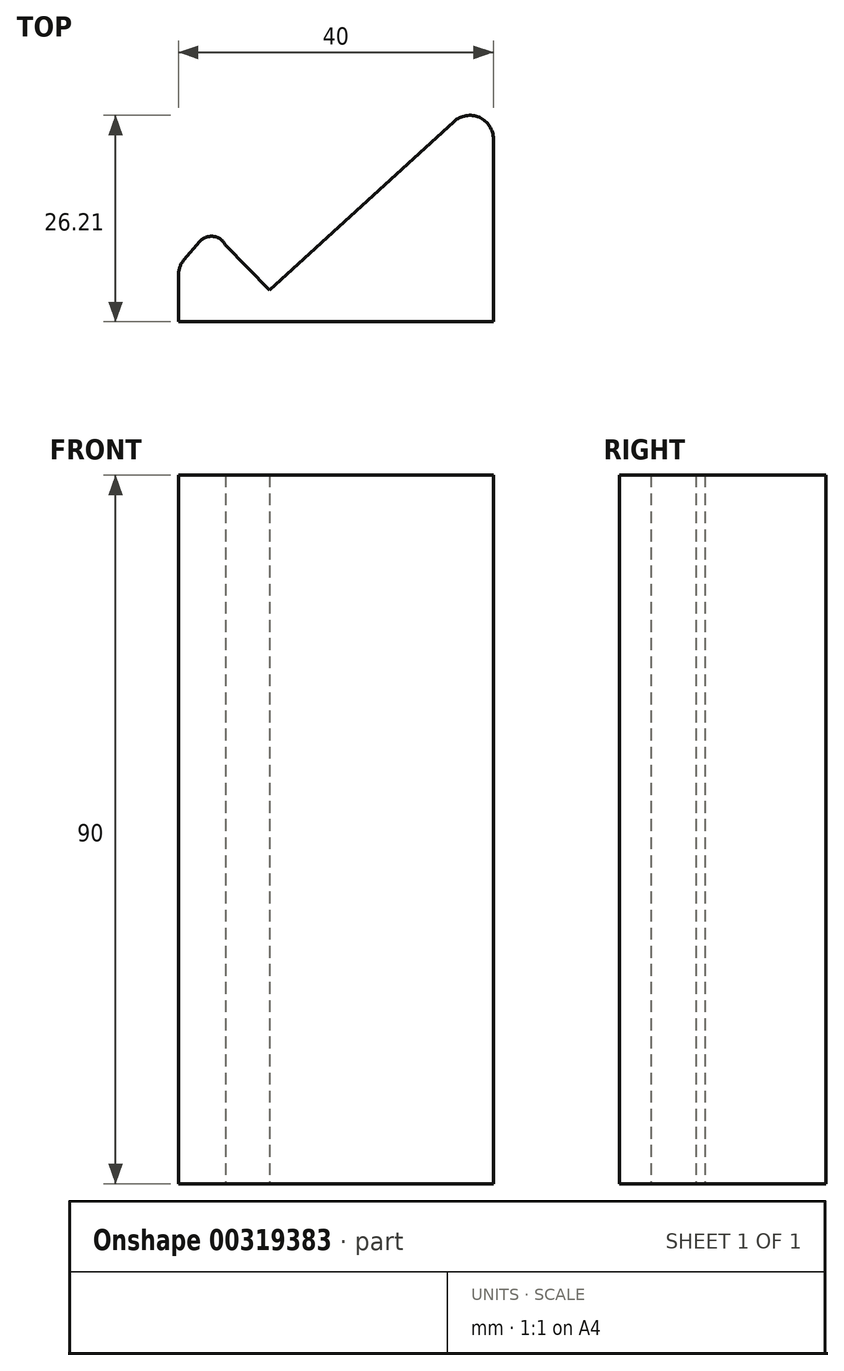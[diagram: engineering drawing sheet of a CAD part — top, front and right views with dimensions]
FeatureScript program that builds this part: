
annotation { "Feature Type Name" : "Feature", "Feature Type Description" : "" }
export const myFeature = defineFeature(function(context is Context, id is Id, definition is map)
    precondition{}
    {
        {
            var Q0;
            Q0=qCreatedBy(makeId("Top.planeOp"),FACE);
            var sketch = newSketch(context, id + "F0", { "sketchPlane" : qUnion([Q0])});
            skLineSegment(sketch, "E0.bottom", {"start": v(20, -17.5) * mm, "end": v(-20, -17.5) * mm});
            skLineSegment(sketch, "E0.top", {"start": v(20, 17.5) * mm, "end": v(-20, 17.5) * mm});
            skLineSegment(sketch, "E0.left", {"start": v(20, -17.5) * mm, "end": v(20, 17.5) * mm});
            skLineSegment(sketch, "E0.right", {"start": v(-20, -17.5) * mm, "end": v(-20, 17.5) * mm});
            skPoint(sketch, "E0.middle", {"position": v(0, 0) * mm});
            skLineSegment(sketch, "E1", {"start": v(-14.02, -7.8) * mm, "end": v(-8.41, -13.5) * mm});
            skLineSegment(sketch, "E2", {"start": v(-8.41, -13.5) * mm, "end": v(20, 12.53) * mm});
            skLineSegment(sketch, "E3", {"start": v(-14.02, -7.8) * mm, "end": v(-14.3, -3.8) * mm});
            skLineSegment(sketch, "E4", {"start": v(-14.3, -3.8) * mm, "end": v(-20, -10.45) * mm});
            skSolve(sketch);
        }
        {
            var Q0;
            {var subQ1=sQuery(id+"F0.wireOp",EDGE,"E0.bottom");Q0=makeQuery(id+"F0.imprint","IMPRINT",FACE,{"disambiguationData":[TD([[makeQuery(id+"F0.imprint","IMPRINT",EDGE,{"derivedFrom":subQ1}),-1.0]])]});}
            extrude(context, id + "F1", {"entities" : qUnion([Q0]), "depth" : 90 * mm});
        }
        {
            var Q0;
            Q0=makeQuery(id+"F1.opExtrude","SWEPT_EDGE",EDGE,{"disambiguationData":[OSD([sQuery(id+"F0.wireOp",EDGE,"E0.right"),sQuery(id+"F0.wireOp",EDGE,"E4")])]});
            var Q1;
            Q1=makeQuery(id+"F1.opExtrude","SWEPT_EDGE",EDGE,{"disambiguationData":[OSD([sQuery(id+"F0.wireOp",EDGE,"E0.left"),sQuery(id+"F0.wireOp",EDGE,"E2")])]});
            fillet(context, id + "F2", {"entities" : qUnion([Q0, Q1]), "radius" : 3 * mm, "tangentPropagation" : true, "allowEdgeOverflow" : false});
        }
        {
            var Q0;
            Q0=makeQuery(id+"F1.opExtrude","SWEPT_EDGE",EDGE,{"disambiguationData":[OSD([sQuery(id+"F0.wireOp",EDGE,"E3"),sQuery(id+"F0.wireOp",EDGE,"E4")])]});
            fillet(context, id + "F3", {"entities" : qUnion([Q0]), "radius" : 2 * mm, "tangentPropagation" : true, "allowEdgeOverflow" : false});
        }
    });
